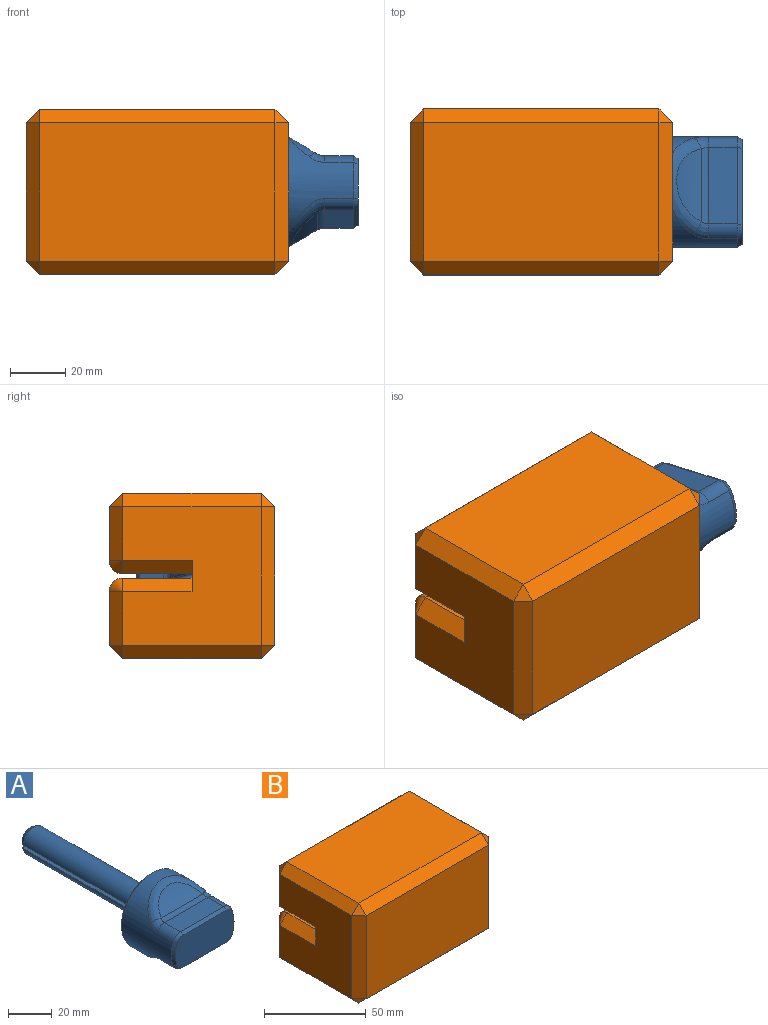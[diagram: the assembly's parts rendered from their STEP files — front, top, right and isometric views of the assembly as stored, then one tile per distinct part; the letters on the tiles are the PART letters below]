
ASSEMBLY  parts=2 mates=1
PART A: 40 faces, bbox 40x113x40 mm
  f0: cylinder r=20mm len=40mm, axis (0,1,0), area 1925.1mm2, adj f11,f22,f23,f24,f25,f26,f27,f28
  f1: plane 38x18mm, normal (0,-1,0), area 652.4mm2, adj f32,f33,f34,f35,f36,f37,f38,f39
  f2: cylinder r=7.25mm len=73mm, axis (0,1,0), area 1516.2mm2, adj f7,f10,f13
  f3: plane 10.61x3.1mm, normal (0,1,0), area 23.3mm2, adj f12,f15
  f4: cylinder r=7.25mm len=73mm, axis (0,1,0), area 1516.2mm2, adj f7,f9,f12
  f5: plane 38x38mm, normal (0,1,0), area 804.1mm2, adj f7,f11
  f6: plane 10.61x3.1mm, normal (0,1,0), area 23.3mm2, adj f13,f14
  f7: torus R=10.25mm, axis (0,-1,0), area 239.3mm2, adj f2,f4,f5,f8,f9,f10
  f8: cylinder r=1mm len=16.03mm, axis (1,0,0), area 48.6mm2, adj f7,f9,f10
  f9: plane 74.01x14.72mm, normal (0,0,1), area 1062.9mm2, adj f4,f7,f8,f15
  f10: plane 74.01x14.72mm, normal (0,0,-1), area 1062.9mm2, adj f2,f7,f8,f14
  f11: cone r=20mm half-angle=45deg, axis (0,-1,0), area 173.3mm2, adj f0,f5
  f12: cone r=7.25mm half-angle=30deg, axis (0,-1,0), area 41.7mm2, adj f3,f4,f15
  f13: cone r=7.25mm half-angle=30deg, axis (0,-1,0), area 41.7mm2, adj f2,f6,f14
  f14: cylinder r=2mm len=14.36mm, axis (1,0,0), area 39.2mm2, adj f6,f10,f13
  f15: cylinder r=2mm len=14.36mm, axis (-1,0,0), area 39.2mm2, adj f3,f9,f12
  f16: cylinder r=5mm len=28.28mm, axis (-1,0,0), area 82.7mm2, adj f17,f18,f28,f31
  f17: cylinder r=50mm len=26.83mm, axis (-1,0,0), area 227.4mm2, adj f16,f30
  f18: plane 28.28x10.28mm, normal (0,0,1), area 290.8mm2, adj f16,f27,f29,f36
  f19: cylinder r=50mm len=26.83mm, axis (-1,0,0), area 227.4mm2, adj f20,f24
  f20: cylinder r=5mm len=28.28mm, axis (-1,0,0), area 82.7mm2, adj f19,f21,f23,f26
  f21: plane 28.28x10.28mm, normal (0,0,-1), area 290.8mm2, adj f20,f22,f25,f35
  f22: cylinder r=5mm len=10.28mm, axis (0,1,0), area 63.3mm2, adj f0,f21,f23,f37
  f23: bspline ~8.14x6.12mm, area 27.1mm2, adj f0,f20,f22,f24
  f24: bspline ~37.95x15.26mm, area 210.3mm2, adj f0,f19,f23,f26
  f25: cylinder r=5mm len=10.28mm, axis (0,1,0), area 63.3mm2, adj f0,f21,f26,f33
  f26: bspline ~8.14x6.12mm, area 27.1mm2, adj f0,f20,f24,f25
  f27: cylinder r=5mm len=10.28mm, axis (0,1,0), area 63.3mm2, adj f0,f18,f28,f34
  f28: bspline ~7.62x6.12mm, area 27.1mm2, adj f0,f16,f27,f30
  f29: cylinder r=5mm len=10.28mm, axis (0,1,0), area 63.3mm2, adj f0,f18,f31,f38
  f30: bspline ~37.95x15.26mm, area 210.3mm2, adj f0,f17,f28,f31
  f31: bspline ~7.62x6.12mm, area 27.1mm2, adj f0,f16,f29,f30
  f32: cone r=19mm half-angle=30deg, axis (0,1,0), area 26.5mm2, adj f0,f1,f33,f34
  f33: cone r=4mm half-angle=30deg, axis (0,1,0), area 11.1mm2, adj f1,f25,f32,f35
  f34: cone r=4mm half-angle=30deg, axis (0,1,0), area 11.1mm2, adj f1,f27,f32,f36
  f35: plane 28.28x1.73mm, normal (0,-0.5,-0.87), area 56.6mm2, adj f1,f21,f33,f37
  f36: plane 28.28x1.73mm, normal (0,-0.5,0.87), area 56.6mm2, adj f1,f18,f34,f38
  f37: cone r=4mm half-angle=30deg, axis (0,1,0), area 11.1mm2, adj f1,f22,f35,f39
  f38: cone r=4mm half-angle=30deg, axis (0,1,0), area 11.1mm2, adj f1,f29,f36,f39
  f39: cone r=19mm half-angle=30deg, axis (0,1,0), area 26.5mm2, adj f0,f1,f37,f38
PART B: 72 faces, bbox 95x60x60 mm
  f0: plane 85x19.25mm, normal (0,1,0), area 1636.2mm2, adj f40,f44,f49,f50
  f1: plane 46.88x40.6mm, normal (1,0,0), area 1142mm2, adj f3,f11,f12,f13,f14,f15,f16,f23
  f2: plane 50x50mm, normal (1,0,0), area 885.8mm2, adj f33,f34,f35,f36,f37,f38,f39,f45
  f3: plane 79x10.97mm, normal (0,-1,0), area 858.6mm2, adj f1,f15,f23,f35,f71
  f4: plane 7x3.75mm, normal (0,-1,0), area 26.3mm2, adj f5,f21,f23,f32
  f5: plane 18.01x15.6mm, normal (1,0,0), area 199.1mm2, adj f4,f17,f18,f19,f20,f21,f22,f23
  f6: plane 50x50mm, normal (-1,0,0), area 2212.5mm2, adj f25,f42,f44,f48,f53,f54,f60,f61
  f7: plane 85x50mm, normal (0,0,-1), area 4250mm2, adj f61,f62,f66,f67
  f8: plane 85x50mm, normal (0,0,1), area 4250mm2, adj f48,f49,f55,f56
  f9: plane 85x50mm, normal (0,-1,0), area 4250mm2, adj f54,f55,f62,f63
  f10: plane 85x19.25mm, normal (0,1,0), area 1636.3mm2, adj f41,f60,f66,f69
  f11: plane 79x20.3mm, normal (0,-0.5,-0.87), area 1851.8mm2, adj f1,f12,f16,f34
  f12: plane 79x20.3mm, normal (0,0.5,-0.87), area 1851.8mm2, adj f1,f11,f13,f36
  f13: plane 79x23.44mm, normal (0,1,0), area 1851.8mm2, adj f1,f12,f14,f38
  f14: plane 79x20.3mm, normal (0,0.5,0.87), area 1851.8mm2, adj f1,f13,f15,f39
  f15: plane 79x20.3mm, normal (0,-0.5,0.87), area 1851.8mm2, adj f1,f3,f14,f37
  f16: plane 79x10.97mm, normal (0,-1,0), area 858.6mm2, adj f1,f11,f24,f33,f45
  f17: plane 7.8x7mm, normal (0,-0.5,-0.87), area 63mm2, adj f5,f18,f22,f27
  f18: plane 7.8x7mm, normal (0,0.5,-0.87), area 63mm2, adj f5,f17,f19,f28
  f19: plane 9.01x7mm, normal (0,1,0), area 63mm2, adj f5,f18,f20,f29
  f20: plane 7.8x7mm, normal (0,0.5,0.87), area 63mm2, adj f5,f19,f21,f30
  f21: plane 7.8x7mm, normal (0,-0.5,0.87), area 63mm2, adj f4,f5,f20,f31
  f22: plane 7x3.75mm, normal (0,-1,0), area 26.3mm2, adj f5,f17,f24,f26
  f23: plane 85x25mm, normal (0,0,1), area 539.6mm2, adj f1,f3,f4,f5,f25,f32,f41,f53
  f24: plane 85x25mm, normal (0,0,-1), area 539.6mm2, adj f1,f5,f16,f22,f25,f26,f40,f42
  f25: plane 11.5x7mm, normal (0,1,0), area 35.5mm2, adj f5,f6,f23,f24,f42,f53
  f26: plane 4.33x1mm, normal (0.71,-0.71,0), area 5.7mm2, adj f1,f22,f24,f27
  f27: plane 8.8x5.66mm, normal (0.71,-0.35,-0.61), area 13.6mm2, adj f1,f17,f26,f28
  f28: plane 8.8x5.66mm, normal (0.71,0.35,-0.61), area 13.6mm2, adj f1,f18,f27,f29
  f29: plane 10.16x1mm, normal (0.71,0.71,0), area 13.6mm2, adj f1,f19,f28,f30
  f30: plane 8.8x5.66mm, normal (0.71,0.35,0.61), area 13.6mm2, adj f1,f20,f29,f31
  f31: plane 8.8x5.66mm, normal (0.71,-0.35,0.61), area 13.6mm2, adj f1,f21,f30,f32
  f32: plane 4.33x1mm, normal (0.71,-0.71,0), area 5.7mm2, adj f1,f4,f23,f31
  f33: plane 7.55x1mm, normal (0.71,-0.71,0), area 9.6mm2, adj f2,f16,f34,f45
  f34: plane 21.3x12.88mm, normal (0.71,-0.35,-0.61), area 34mm2, adj f2,f11,f33,f36
  f35: plane 7.55x1mm, normal (0.71,-0.71,0), area 9.6mm2, adj f2,f3,f37,f71
  f36: plane 21.3x12.88mm, normal (0.71,0.35,-0.61), area 34mm2, adj f2,f12,f34,f38
  f37: plane 21.3x12.88mm, normal (0.71,-0.35,0.61), area 34mm2, adj f2,f15,f35,f39
  f38: plane 24.6x1mm, normal (0.71,0.71,0), area 34mm2, adj f2,f13,f36,f39
  f39: plane 21.3x12.88mm, normal (0.71,0.35,0.61), area 34mm2, adj f2,f14,f37,f38
  f40: cylinder r=5mm len=85mm, axis (1,0,0), area 667.6mm2, adj f0,f24,f43,f47
  f41: cylinder r=5mm len=85mm, axis (-1,0,0), area 667.6mm2, adj f10,f23,f57,f70
  f42: plane 25x5mm, normal (-0.71,0,-0.71), area 176.8mm2, adj f6,f24,f25,f43
  f43: cone r=5mm half-angle=45deg, axis (1,0,0), area 27.8mm2, adj f40,f42,f44
  f44: plane 19.25x5mm, normal (-0.71,0.71,0), area 136.1mm2, adj f0,f6,f43,f46
  f45: plane 5x5mm, normal (0.71,0,-0.71), area 32.5mm2, adj f2,f16,f24,f33,f47
  f46: plane 5x5mm, normal (-0.58,0.58,0.58), area 21.7mm2, adj f44,f48,f49
  f47: cone r=5mm half-angle=45deg, axis (-1,0,0), area 27.8mm2, adj f40,f45,f50
  f48: plane 50x5mm, normal (-0.71,0,0.71), area 353.6mm2, adj f6,f8,f46,f51
  f49: plane 85x5mm, normal (0,0.71,0.71), area 601mm2, adj f0,f8,f46,f52
  f50: plane 19.25x5mm, normal (0.71,0.71,0), area 136.1mm2, adj f0,f2,f47,f52
  f51: plane 5x5mm, normal (-0.58,-0.58,0.58), area 21.7mm2, adj f48,f54,f55
  f52: plane 5x5mm, normal (0.58,0.58,0.58), area 21.7mm2, adj f49,f50,f56
  f53: plane 25x5mm, normal (-0.71,0,0.71), area 176.8mm2, adj f6,f23,f25,f57
  f54: plane 50x5mm, normal (-0.71,-0.71,0), area 353.6mm2, adj f6,f9,f51,f58
  f55: plane 85x5mm, normal (0,-0.71,0.71), area 601mm2, adj f8,f9,f51,f59
  f56: plane 50x5mm, normal (0.71,0,0.71), area 353.6mm2, adj f2,f8,f52,f59
  f57: cone r=5mm half-angle=45deg, axis (1,0,0), area 27.8mm2, adj f41,f53,f60
  f58: plane 5x5mm, normal (-0.58,-0.58,-0.58), area 21.7mm2, adj f54,f61,f62
  f59: plane 5x5mm, normal (0.58,-0.58,0.58), area 21.7mm2, adj f55,f56,f63
  f60: plane 19.25x5mm, normal (-0.71,0.71,0), area 136.1mm2, adj f6,f10,f57,f64
  f61: plane 50x5mm, normal (-0.71,0,-0.71), area 353.6mm2, adj f6,f7,f58,f64
  f62: plane 85x5mm, normal (0,-0.71,-0.71), area 601mm2, adj f7,f9,f58,f65
  f63: plane 50x5mm, normal (0.71,-0.71,0), area 353.6mm2, adj f2,f9,f59,f65
  f64: plane 5x5mm, normal (-0.58,0.58,-0.58), area 21.7mm2, adj f60,f61,f66
  f65: plane 5x5mm, normal (0.58,-0.58,-0.58), area 21.7mm2, adj f62,f63,f67
  f66: plane 85x5mm, normal (0,0.71,-0.71), area 601mm2, adj f7,f10,f64,f68
  f67: plane 50x5mm, normal (0.71,0,-0.71), area 353.6mm2, adj f2,f7,f65,f68
  f68: plane 5x5mm, normal (0.58,0.58,-0.58), area 21.7mm2, adj f66,f67,f69
  f69: plane 19.25x5mm, normal (0.71,0.71,0), area 136.1mm2, adj f2,f10,f68,f70
  f70: cone r=5mm half-angle=45deg, axis (-1,0,0), area 27.8mm2, adj f41,f69,f71
  f71: plane 5x5mm, normal (0.71,0,0.71), area 32.5mm2, adj f2,f3,f23,f35,f70
PLACE A rot(axis=(0.7,-0.7,0.08),170.9deg) t=(2.5,0,0)mm
PLACE B at identity fixed
MATE revolute A.f0 <-> B.f5  axis (-1,0,0) through (-40.5,0,0)mm
